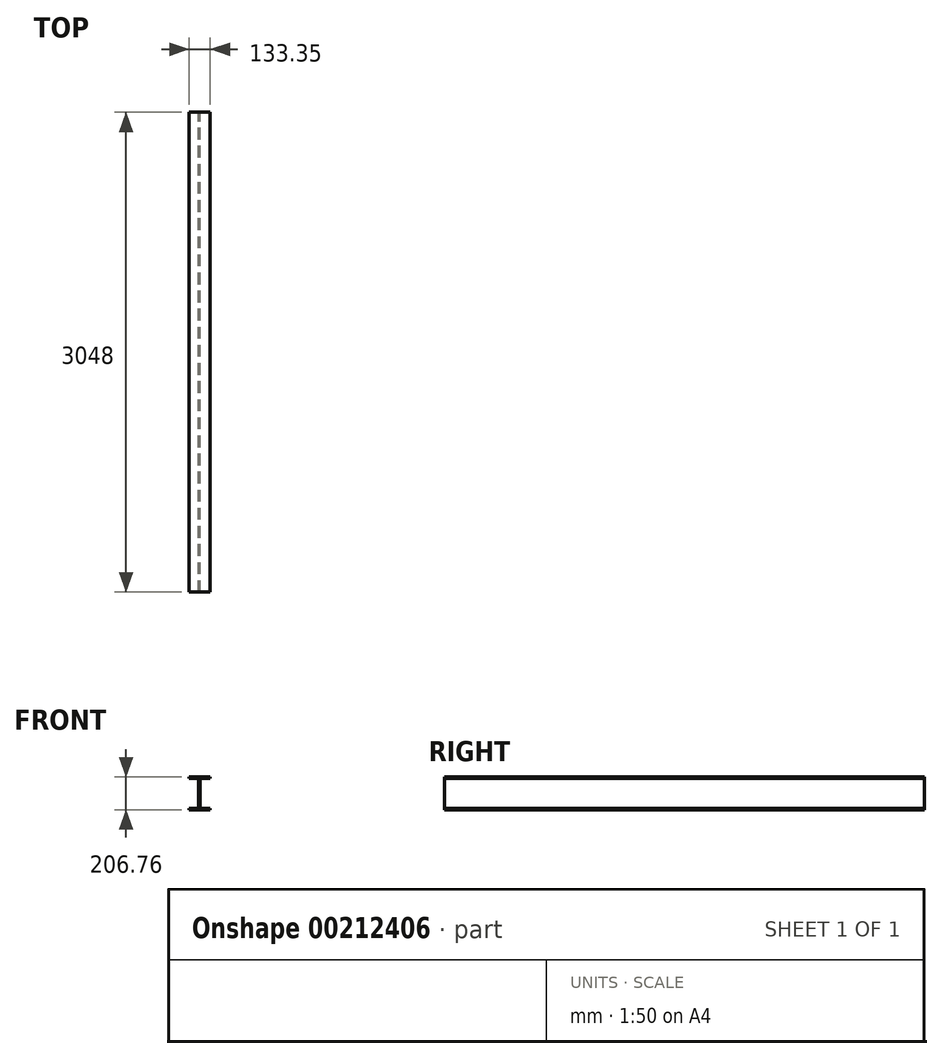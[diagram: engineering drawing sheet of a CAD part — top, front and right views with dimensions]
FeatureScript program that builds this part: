
annotation { "Feature Type Name" : "Feature", "Feature Type Description" : "" }
export const myFeature = defineFeature(function(context is Context, id is Id, definition is map)
    precondition{}
    {
        {
            var Q0;
            Q0=qCreatedBy(makeId("Front.planeOp"),FACE);
            var sketch = newSketch(context, id + "F0", { "sketchPlane" : qUnion([Q0])});
            skLineSegment(sketch, "E0", {"start": v(0, 0) * mm, "end": v(-170.11, 0) * mm});
            skLineSegment(sketch, "E1", {"start": v(-170.11, 0) * mm, "end": v(-170.11, 7.94) * mm});
            skLineSegment(sketch, "E2", {"start": v(-170.11, 7.94) * mm, "end": v(-109.56, 7.94) * mm});
            skLineSegment(sketch, "E3", {"start": v(-109.56, 7.94) * mm, "end": v(-109.56, 198.82) * mm});
            skLineSegment(sketch, "E4", {"start": v(-109.56, 198.82) * mm, "end": v(-170.11, 198.82) * mm});
            skLineSegment(sketch, "E5", {"start": v(-170.11, 198.82) * mm, "end": v(-170.11, 206.76) * mm});
            skLineSegment(sketch, "E6", {"start": v(-170.11, 206.76) * mm, "end": v(-36.76, 206.76) * mm});
            skLineSegment(sketch, "E7", {"start": v(-36.76, 206.76) * mm, "end": v(-36.76, 198.82) * mm});
            skLineSegment(sketch, "E8", {"start": v(-36.76, 198.82) * mm, "end": v(-101.63, 198.82) * mm});
            skLineSegment(sketch, "E9", {"start": v(-101.63, 198.82) * mm, "end": v(-101.63, 7.94) * mm});
            skLineSegment(sketch, "E10", {"start": v(-101.63, 7.94) * mm, "end": v(-36.76, 7.94) * mm});
            skLineSegment(sketch, "E11", {"start": v(-36.76, 7.94) * mm, "end": v(-36.76, 0) * mm});
            skLineSegment(sketch, "E12", {"start": v(-36.76, 0) * mm, "end": v(-170.11, 0) * mm});
            skSolve(sketch);
        }
        {
            var Q0;
            Q0 = qSketchRegion(id + "F0", true);
            extrude(context, id + "F1", {"entities" : qUnion([Q0]), "depth" : 3048 * mm});
        }
    });
